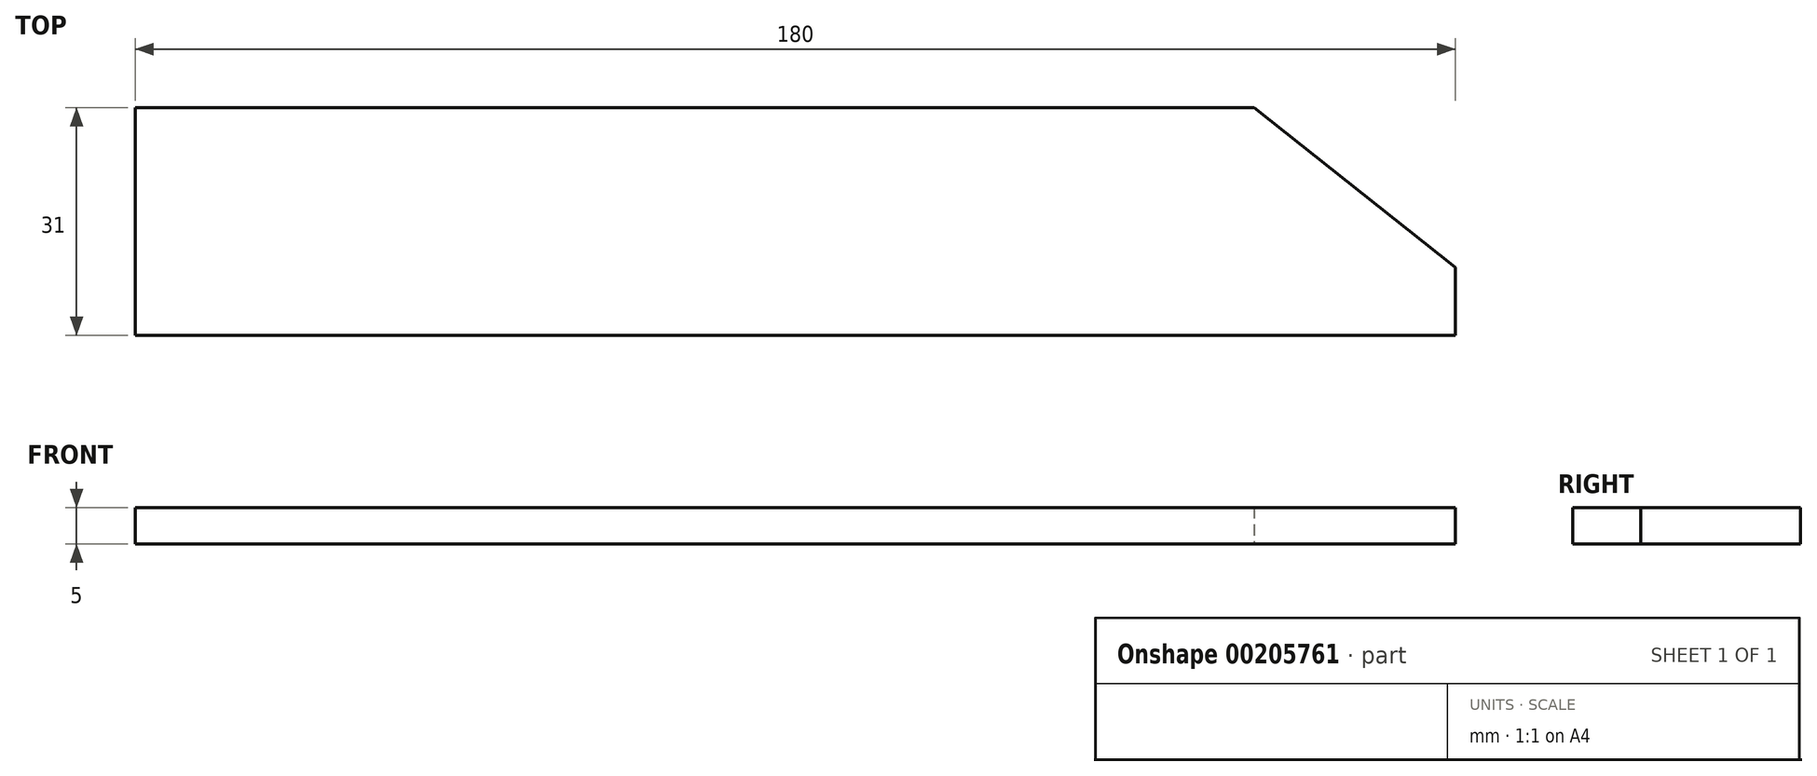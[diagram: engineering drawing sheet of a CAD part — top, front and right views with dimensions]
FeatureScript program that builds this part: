
annotation { "Feature Type Name" : "Feature", "Feature Type Description" : "" }
export const myFeature = defineFeature(function(context is Context, id is Id, definition is map)
    precondition{}
    {
        {
            var Q0;
            Q0=qCreatedBy(makeId("Top.planeOp"),FACE);
            var sketch = newSketch(context, id + "F0", { "sketchPlane" : qUnion([Q0])});
            skLineSegment(sketch, "E0.top", {"start": v(-56.37, 24.64) * mm, "end": v(123.63, 24.64) * mm});
            skLineSegment(sketch, "E0.left", {"start": v(-56.37, 55.64) * mm, "end": v(-56.37, 24.64) * mm});
            skLineSegment(sketch, "E1", {"start": v(123.63, 33.9) * mm, "end": v(96.16, 55.64) * mm});
            skLineSegment(sketch, "E2", {"start": v(-56.37, 55.64) * mm, "end": v(96.16, 55.64) * mm});
            skLineSegment(sketch, "E3", {"start": v(123.63, 33.9) * mm, "end": v(123.63, 24.64) * mm});
            skSolve(sketch);
        }
        {
            var Q0;
            Q0 = qSketchRegion(id + "F0", true);
            extrude(context, id + "F1", {"entities" : qUnion([Q0]), "endBound" : BoundingType.SYMMETRIC, "depth" : 5 * mm});
        }
    });
